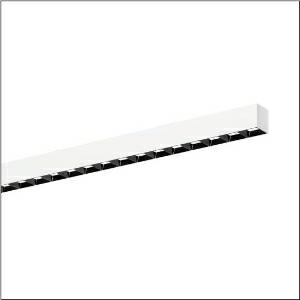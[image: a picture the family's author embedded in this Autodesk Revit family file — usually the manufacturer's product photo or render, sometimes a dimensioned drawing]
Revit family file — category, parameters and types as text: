
# Revit family: silica_21_51mx24dc3awb
name_source: partatom
category: Lighting Fixtures
units: mm (PartAtom-declared; Revit-internal decimal feet)

## family parameters
Cut with Voids When Loaded = No
Host = Face
Light Source = No
Part Type = Normal
Room Calculation Point = No
Round Connector Dimension = Use Diameter
Shared = No

## types (1)
- --- (1 x LED, 10800 lm, 79 W, 3000K)
    Apparent Load = 79 VA
    CIE Flux Codes = 74 94 99 100 100
    Color Rendering = 80
    Color Temperature = 3000K
    Default Elevation = 1800 mm
    Description = Silica 21, office luminaire, primary light control with darklight reflector, of PMMA, black, CAT 2 (L<= 3000cd/m²), light emission: direct distribution, primary light characteristic: asymmetric, installation type: surface-mounted, LED, rated luminous flux: 10.800lm, luminous efficacy: 137lm/W, light colour: 830, colour temperature: 3000K, control gear: DALI 2, with terminal, 3+2-pole, max. 2.5mm², mains connection: 220..240V, AC, 50/60Hz, rated input power: 79W, luminaire housing, of aluminium, traffic white (RAL 9016), length: 3.004mm, width: 53mm, height: 53mm, protection rating (complete): IP20, insulation class (complete): insulation class I (protective earthing), certification: CE, permissible operating ambient temperature: 0..+35°C, standard: EN 50419, packaging unit: 1 piece
    Height = 53 mm
    Lamp = 1 x LED
    Lamp Light Flux = 10800 lm
    Lamp Power = 79 W
    Lamp count = 1
    Length = 3004 mm
    Luminous efficacy = 137 lm/W
    Manufacturer = Siteco
    ModVariant = No
    Model = 51MX24DC3AWB
    Mounting Place = Ceiling
    Mounting Type = Surface mounted
    Number of Poles = 1
    OnlyDefault = Yes
    Power Factor = 1
    Product Name = Silica 21
    Product group = office luminaire | ceiling mounted
    ProductGroupID = 301
    Protection Class = Protection class I
    Protection Degree = IP 20
    RLX_Detail_Level = 1
    RLX_Emergency_Light_Flux = 0 lm
    RLX_Emergency_Type = 0
    RLX_Emergency_Type_DB = No
    RlxData = <blob elided: 64837 chars, md5=60a6ef4f>
    Socket = socket
    Standby Power = 0 W
    System Light Flux = 10800 lm
    System Power = 79 W
    Type Comments = factory setting: luminous flux: 100 % | dim-lin: 254 | 448 mA
    Type Image = l_1335873.jpg
    URL = http://relux.com
    VarID = @adj_123243
    Voltage = 0 V
    Weight = 0.00 kg
    Width = 53 mm

## geometry (parser evidence)
native form markers: Blend x4, Sweep x10
no freeform markers — native parametric forms only
